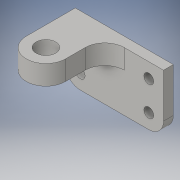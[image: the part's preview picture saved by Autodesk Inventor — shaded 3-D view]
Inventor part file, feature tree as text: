
AUTODESK INVENTOR PART (.ipt)
format: ipt  version: 2016 (Build 200138000, 138)  size: 138,752 bytes
history: native  units: in
note: dims shown in document units (in); Inventor stores cm internally (conversion verified against a paired STEP export)
features: sketch x4, extrude x2, fillet x2, hole x2
ambient origin geometry x8: Origin, YZ Plane, XZ Plane, XY Plane, X Axis, Y Axis, Z Axis, Center Point
bodies: Solid1 (feature_tree)
feature tree (10):
  extrude  "Extrusion1"  Depth=1.5in
  fillet  "Fillet1"  Radius=0.25in
  hole  "Hole1"  [1 undecoded]
  extrude  "Extrusion2"  Depth=0.5in
  fillet  "Fillet2"  Radius=1.0in
  hole  "Hole2"  [1 undecoded]
  sketch  "Sketch1"  dims[d0=2.5in d1=1.5in d2=0.25in d3=0.0in]
  sketch  "Sketch2"  dims[d4=0.375in d5=0.375in]
  sketch  "Sketch3"  dims[d6=0.375in]
  sketch  "Sketch4"  dims[d7=0.25in d8=0.75in d9=0.375in d10=0.25in d11=0.5635in d12=1.0in d13=0.8108in d14=0.5in d15=1.0in d16=1.5in d17=0.0in d18=0.5in d19=0.5in d20=0.75in d21=0.375in d22=0.25in d23=0.5635in d24=1.0in d25=0.8108in]
note: 2 required parameter values undecoded (feature->parameter linkage not recoverable at this tier; creation-order binding heuristic only, values carry confidence <= 0.55)
